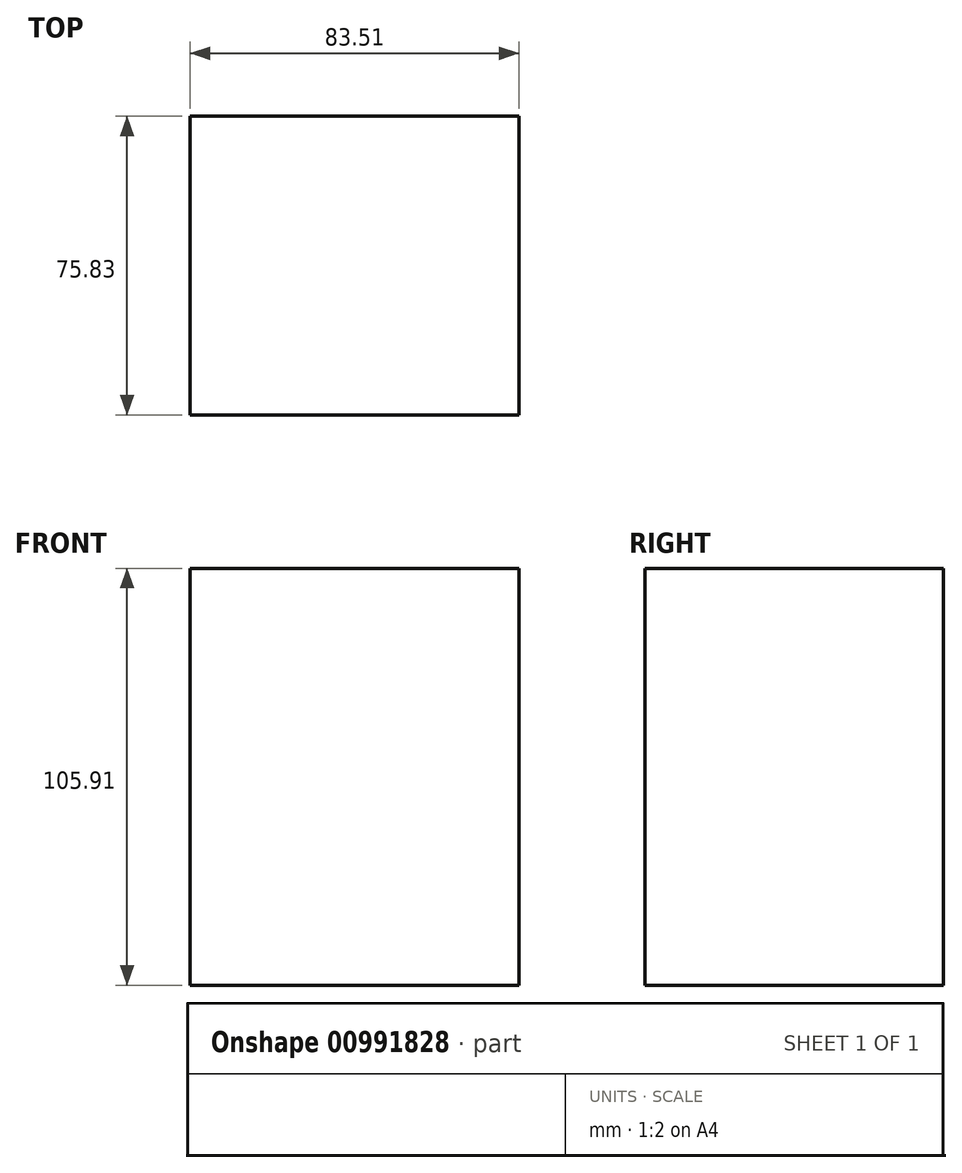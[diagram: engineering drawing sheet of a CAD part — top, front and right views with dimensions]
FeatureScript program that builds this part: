
annotation { "Feature Type Name" : "Feature", "Feature Type Description" : "" }
export const myFeature = defineFeature(function(context is Context, id is Id, definition is map)
    precondition{}
    {
        {
            var Q0;
            Q0=qCreatedBy(makeId("Front.planeOp"),FACE);
            var sketch = newSketch(context, id + "F0", { "sketchPlane" : qUnion([Q0])});
            skLineSegment(sketch, "E0.bottom", {"start": v(-42.08, 55.17) * mm, "end": v(41.43, 55.17) * mm});
            skLineSegment(sketch, "E0.top", {"start": v(-42.08, -50.74) * mm, "end": v(41.43, -50.74) * mm});
            skLineSegment(sketch, "E0.left", {"start": v(-42.08, 55.17) * mm, "end": v(-42.08, -50.74) * mm});
            skLineSegment(sketch, "E0.right", {"start": v(41.43, 55.17) * mm, "end": v(41.43, -50.74) * mm});
            skSolve(sketch);
        }
        {
            var Q0;
            Q0=makeQuery(id+"F0.imprint","IMPRINT",FACE,{"disambiguationData":[TD([[makeQuery(id+"F0.imprint","IMPRINT",EDGE,{"derivedFrom":sQuery(id+"F0.wireOp",EDGE,"E0.bottom")}),-1.0]])]});
            extrude(context, id + "F1", {"entities" : qUnion([Q0]), "depth" : 75.83 * mm, "offsetDistance" : 25.4 * mm});
        }
    });
